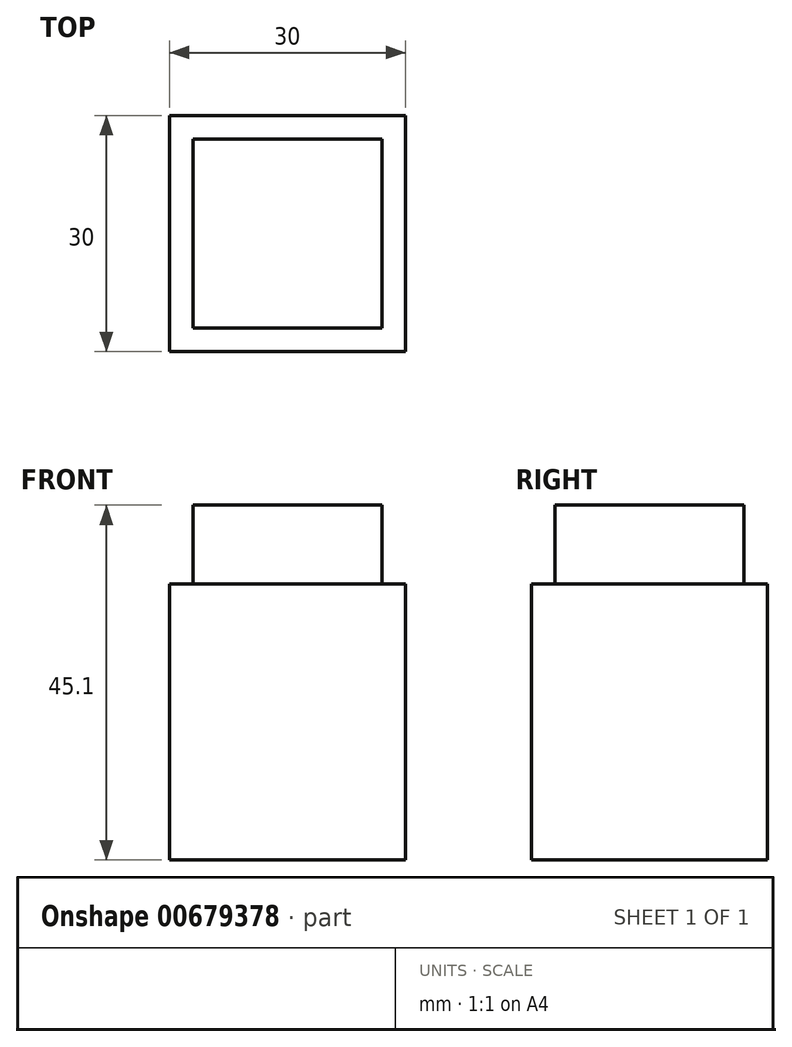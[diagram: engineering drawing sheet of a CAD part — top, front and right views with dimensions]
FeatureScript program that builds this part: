
annotation { "Feature Type Name" : "Feature", "Feature Type Description" : "" }
export const myFeature = defineFeature(function(context is Context, id is Id, definition is map)
    precondition{}
    {
        {
            var Q0;
            Q0=qCreatedBy(makeId("Top.planeOp"),FACE);
            var sketch = newSketch(context, id + "F0", { "sketchPlane" : qUnion([Q0])});
            skLineSegment(sketch, "E0.bottom", {"start": v(15, 15) * mm, "end": v(-15, 15) * mm});
            skLineSegment(sketch, "E0.top", {"start": v(15, -15) * mm, "end": v(-15, -15) * mm});
            skLineSegment(sketch, "E0.left", {"start": v(15, 15) * mm, "end": v(15, -15) * mm});
            skLineSegment(sketch, "E0.right", {"start": v(-15, 15) * mm, "end": v(-15, -15) * mm});
            skPoint(sketch, "E0.middle", {"position": v(0, 0) * mm});
            skSolve(sketch);
        }
        {
            var Q0;
            Q0 = qSketchRegion(id + "F0", true);
            extrude(context, id + "F1", {"entities" : qUnion([Q0]), "depth" : 35.1 * mm, "offsetDistance" : 25 * mm});
        }
        {
            var Q0;
            Q0=makeQuery(id+"F1.opExtrude","CAP_FACE",FACE,{"disambiguationData":[OSD([sQuery(id+"F0.wireOp",EDGE,"E0.bottom"),sQuery(id+"F0.wireOp",EDGE,"E0.top"),sQuery(id+"F0.wireOp",EDGE,"E0.left"),sQuery(id+"F0.wireOp",EDGE,"E0.right")])],"isStart":false});
            var sketch = newSketch(context, id + "F2", { "sketchPlane" : qUnion([Q0])});
            skLineSegment(sketch, "E1.bottom", {"start": v(-12, 12) * mm, "end": v(12, 12) * mm});
            skLineSegment(sketch, "E1.top", {"start": v(-12, -12) * mm, "end": v(12, -12) * mm});
            skLineSegment(sketch, "E1.left", {"start": v(-12, 12) * mm, "end": v(-12, -12) * mm});
            skLineSegment(sketch, "E1.right", {"start": v(12, 12) * mm, "end": v(12, -12) * mm});
            skSolve(sketch);
        }
        {
            var Q0;
            Q0 = qSketchRegion(id + "F2", true);
            extrude(context, id + "F3", {"entities" : qUnion([Q0]), "operationType" : NewBodyOperationType.ADD, "oppositeDirection" : true, "depth" : -10 * mm, "offsetDistance" : 25 * mm});
        }
    });
